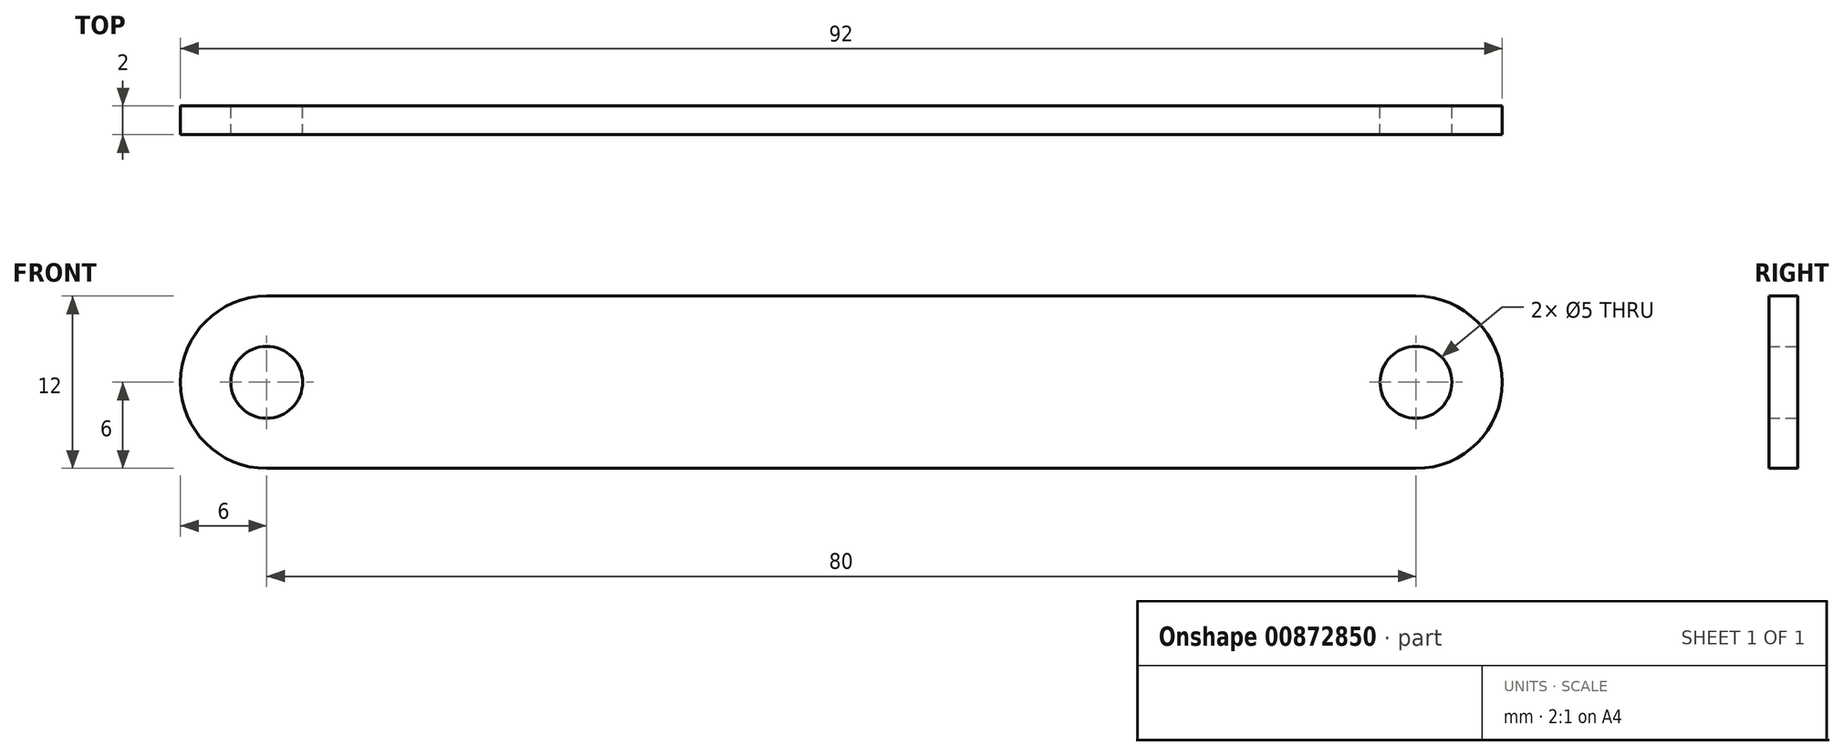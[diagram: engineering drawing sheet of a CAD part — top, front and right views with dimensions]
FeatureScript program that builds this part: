
annotation { "Feature Type Name" : "Feature", "Feature Type Description" : "" }
export const myFeature = defineFeature(function(context is Context, id is Id, definition is map)
    precondition{}
    {
        {
            var Q0;
            Q0=qCreatedBy(makeId("Front.planeOp"),FACE);
            var sketch = newSketch(context, id + "F0", { "sketchPlane" : qUnion([Q0])});
            skArc(sketch, "E0", {"start": v(0, 6) * mm, "mid": v(-6, 0) * mm, "end": v(0, -6) * mm});
            skCircle(sketch, "E1", {"center": v(0, 0) * mm, "radius": 2.5 * mm});
            skArc(sketch, "E2", {"start": v(80, -6) * mm, "mid": v(86, 0) * mm, "end": v(80, 6) * mm});
            skCircle(sketch, "E3", {"center": v(80, 0) * mm, "radius": 2.5 * mm});
            skLineSegment(sketch, "E4", {"start": v(0, 6) * mm, "end": v(80, 6) * mm});
            skLineSegment(sketch, "E5", {"start": v(0, -6) * mm, "end": v(80, -6) * mm});
            skSolve(sketch);
        }
        {
            var Q0;
            Q0 = qSketchRegion(id + "F0", true);
            extrude(context, id + "F1", {"entities" : qUnion([Q0]), "depth" : 2 * mm, "offsetDistance" : 25 * mm});
        }
    });
